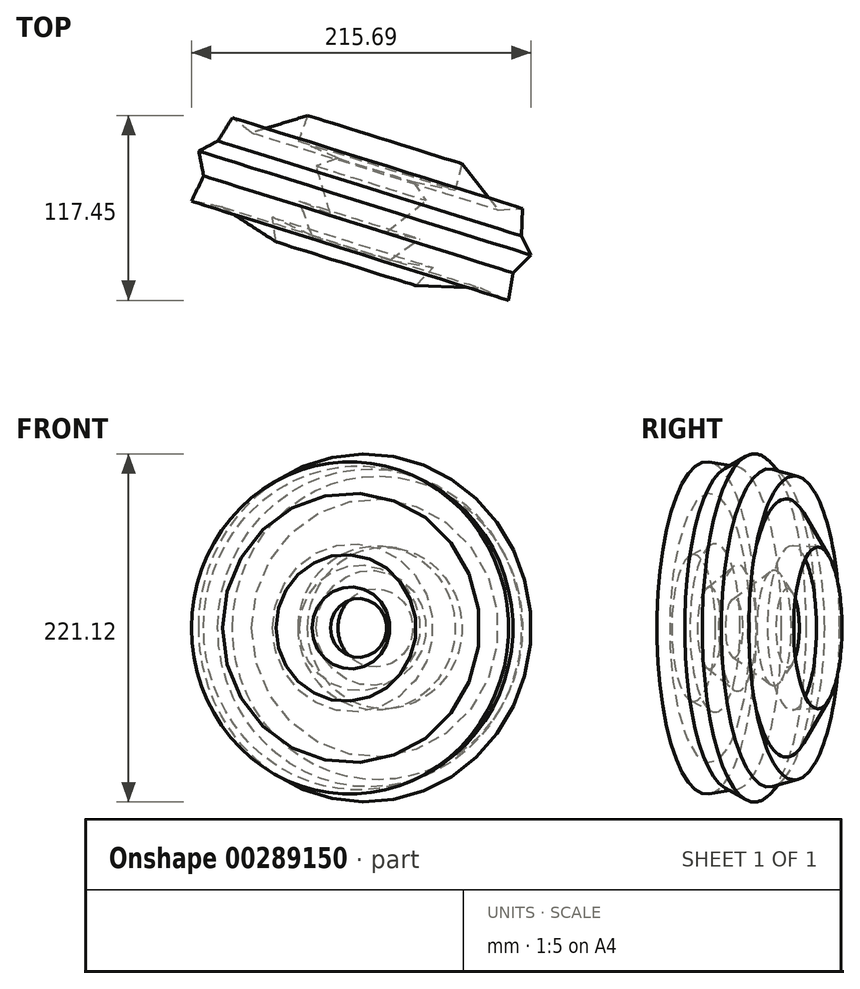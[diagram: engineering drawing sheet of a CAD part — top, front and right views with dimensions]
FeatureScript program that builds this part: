
annotation { "Feature Type Name" : "Feature", "Feature Type Description" : "" }
export const myFeature = defineFeature(function(context is Context, id is Id, definition is map)
    precondition{}
    {
        {
            var Q0;
            Q0=qCreatedBy(makeId("Top.planeOp"),FACE);
            var sketch = newSketch(context, id + "F0", { "sketchPlane" : qUnion([Q0])});
            skLineSegment(sketch, "E0", {"start": v(-127.4, -22.44) * mm, "end": v(-115.36, -15.98) * mm});
            skLineSegment(sketch, "E1", {"start": v(-115.36, -15.98) * mm, "end": v(-106.02, -1.25) * mm});
            skLineSegment(sketch, "E2", {"start": v(-106.02, -1.25) * mm, "end": v(-93.8, -10.77) * mm});
            skLineSegment(sketch, "E3", {"start": v(-93.8, -10.77) * mm, "end": v(-58.25, 0.19) * mm});
            skLineSegment(sketch, "E4", {"start": v(-58.25, 0.19) * mm, "end": v(-64.18, -15.98) * mm});
            skLineSegment(sketch, "E5", {"start": v(-64.18, -15.98) * mm, "end": v(-39.03, -26.93) * mm});
            skLineSegment(sketch, "E6", {"start": v(-39.03, -26.93) * mm, "end": v(-52.86, -31.96) * mm});
            skLineSegment(sketch, "E7", {"start": v(-52.86, -31.96) * mm, "end": v(-43.7, -62.67) * mm});
            skLineSegment(sketch, "E8", {"start": v(-43.7, -62.67) * mm, "end": v(-63.46, -54.23) * mm});
            skLineSegment(sketch, "E9", {"start": v(-63.46, -54.23) * mm, "end": v(-55.55, -76.14) * mm});
            skLineSegment(sketch, "E10", {"start": v(-55.55, -76.14) * mm, "end": v(-80.7, -64.47) * mm});
            skLineSegment(sketch, "E11", {"start": v(-80.7, -64.47) * mm, "end": v(-78.36, -80.09) * mm});
            skLineSegment(sketch, "E12", {"start": v(-78.36, -80.09) * mm, "end": v(-112.48, -58) * mm});
            skLineSegment(sketch, "E13", {"start": v(-112.48, -58) * mm, "end": v(-132.06, -54.23) * mm});
            skLineSegment(sketch, "E14", {"start": v(-132.06, -54.23) * mm, "end": v(-124.34, -38.25) * mm});
            skLineSegment(sketch, "E15", {"start": v(-124.34, -38.25) * mm, "end": v(-127.4, -22.44) * mm});
            skLineSegment(sketch, "E16", {"start": v(-17.2, -40.52) * mm, "end": v(-24.82, -64.84) * mm});
            skSolve(sketch);
        }
        {
            var Q0;
            Q0=makeQuery(id+"F0.imprint","IMPRINT",FACE,{"disambiguationData":[TD([[makeQuery(id+"F0.imprint","IMPRINT",EDGE,{"derivedFrom":sQuery(id+"F0.wireOp",EDGE,"E0")}),-1.0]])]});
            var Q1;
            Q1=sQuery(id+"F0.wireOp",EDGE,"E16");
            revolve(context, id + "F1", {"entities" : qUnion([Q0]), "axis" : qUnion([Q1]), "revolveType" : RevolveType.FULL});
        }
    });
